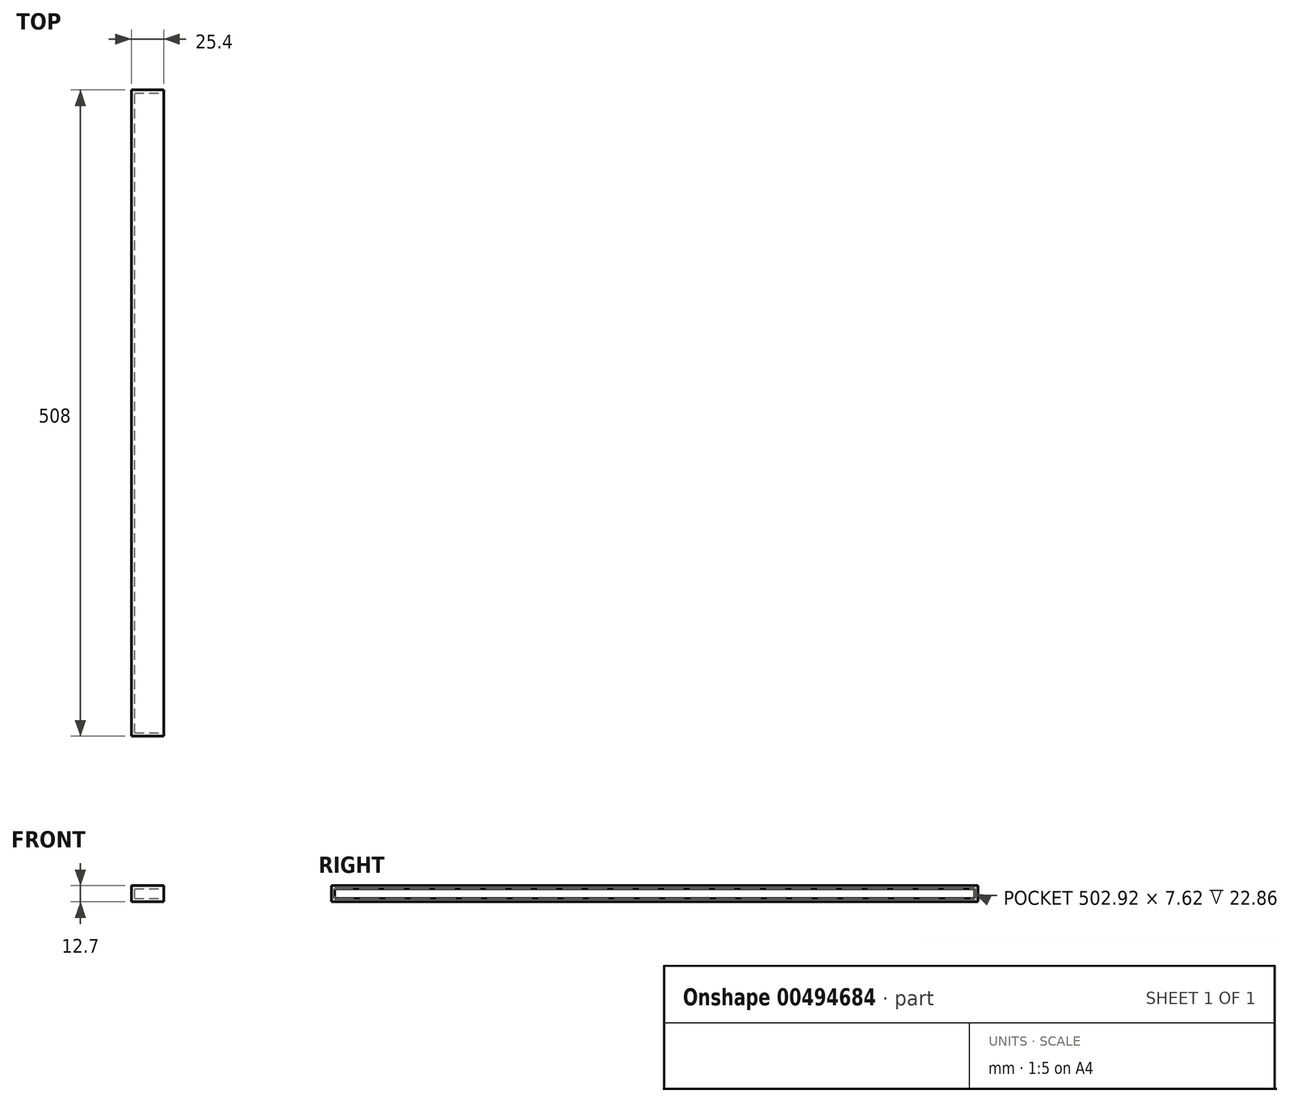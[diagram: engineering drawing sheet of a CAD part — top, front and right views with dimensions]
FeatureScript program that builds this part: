
annotation { "Feature Type Name" : "Feature", "Feature Type Description" : "" }
export const myFeature = defineFeature(function(context is Context, id is Id, definition is map)
    precondition{}
    {
        {
            var Q0;
            Q0=qCreatedBy(makeId("Front.planeOp"),FACE);
            var sketch = newSketch(context, id + "F0", { "sketchPlane" : qUnion([Q0])});
            skLineSegment(sketch, "E0.bottom", {"start": v(0, 0) * mm, "end": v(25.4, 0) * mm});
            skLineSegment(sketch, "E0.top", {"start": v(0, 12.7) * mm, "end": v(25.4, 12.7) * mm});
            skLineSegment(sketch, "E0.left", {"start": v(0, 0) * mm, "end": v(0, 12.7) * mm});
            skLineSegment(sketch, "E0.right", {"start": v(25.4, 0) * mm, "end": v(25.4, 12.7) * mm});
            skSolve(sketch);
        }
        {
            var Q0;
            Q0 = qSketchRegion(id + "F0", true);
            extrude(context, id + "F1", {"entities" : qUnion([Q0]), "depth" : 508 * mm});
        }
        {
            var Q0;
            Q0=makeQuery(id+"F1.opExtrude","SWEPT_FACE",FACE,{"disambiguationData":[OSD([sQuery(id+"F0.wireOp",EDGE,"E0.right")])]});
            var sketch = newSketch(context, id + "F2", { "sketchPlane" : qUnion([Q0])});
            skLineSegment(sketch, "E1.0", {"start": v(-2.54, 2.54) * mm, "end": v(-2.54, 10.16) * mm});
            skLineSegment(sketch, "E1.1", {"start": v(-505.46, 2.54) * mm, "end": v(-2.54, 2.54) * mm});
            skLineSegment(sketch, "E1.2", {"start": v(-505.46, 10.16) * mm, "end": v(-505.46, 2.54) * mm});
            skLineSegment(sketch, "E1.3", {"start": v(-2.54, 10.16) * mm, "end": v(-505.46, 10.16) * mm});
            skSolve(sketch);
        }
        {
            var Q0;
            Q0 = qSketchRegion(id + "F2", true);
            extrude(context, id + "F3", {"entities" : qUnion([Q0]), "operationType" : NewBodyOperationType.REMOVE, "oppositeDirection" : true, "depth" : 22.86 * mm});
        }
    });
